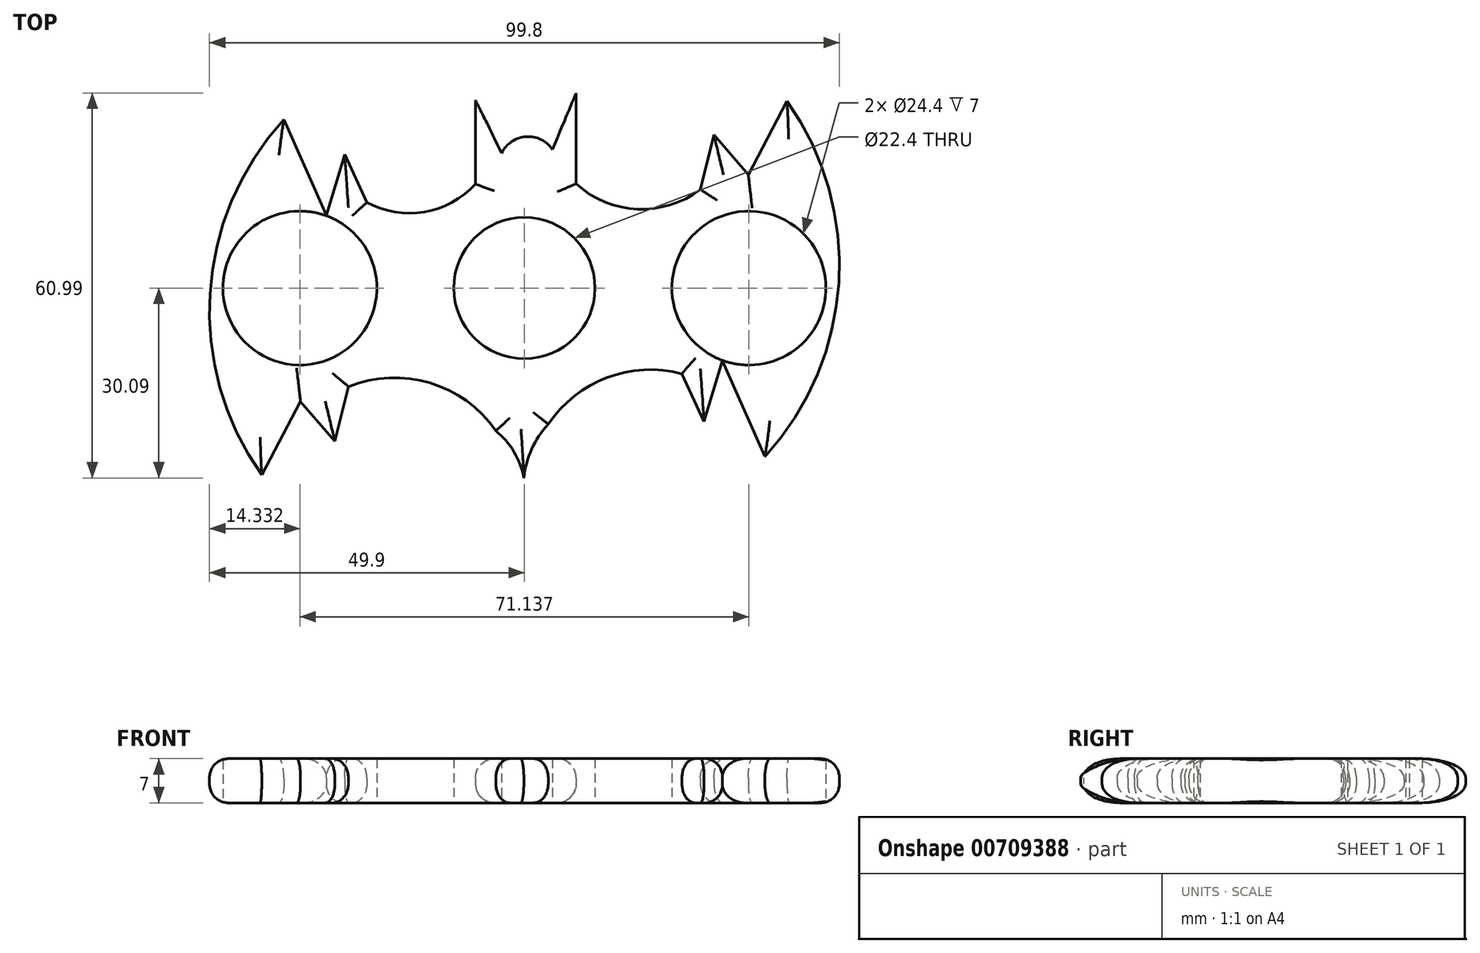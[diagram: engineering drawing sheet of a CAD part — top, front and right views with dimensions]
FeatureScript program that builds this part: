
annotation { "Feature Type Name" : "Feature", "Feature Type Description" : "" }
export const myFeature = defineFeature(function(context is Context, id is Id, definition is map)
    precondition{}
    {
        {
            var Q0;
            Q0=qCreatedBy(makeId("Top.planeOp"),FACE);
            var sketch = newSketch(context, id + "F0", { "sketchPlane" : qUnion([Q0])});
            skCircle(sketch, "E0", {"center": v(0, 0) * mm, "radius": 11.2 * mm});
            skCircle(sketch, "E1", {"center": v(0, 0) * mm, "radius": 13.2 * mm});
            skArc(sketch, "E2", {"start": v(-38.1, 26.72) * mm, "mid": v(-49.82, -0.84) * mm, "end": v(-41.61, -29.64) * mm});
            skArc(sketch, "E3.1.0", {"start": v(38.1, -26.72) * mm, "mid": v(49.82, 0.84) * mm, "end": v(41.61, 29.64) * mm});
            skLineSegment(sketch, "E4", {"start": v(-41.61, -29.64) * mm, "end": v(-35.48, -17.96) * mm});
            skLineSegment(sketch, "E5", {"start": v(-35.48, -17.96) * mm, "end": v(-35.48, -24.97) * mm});
            skArc(sketch, "E6", {"start": v(-4.53, -22.63) * mm, "mid": v(-14.98, -15.03) * mm, "end": v(-27.89, -15.62) * mm});
            skLineSegment(sketch, "E7.1.0", {"start": v(41.61, 29.64) * mm, "end": v(35.48, 17.96) * mm});
            skLineSegment(sketch, "E7.1.1", {"start": v(35.48, 17.96) * mm, "end": v(30.03, 24.29) * mm});
            skLineSegment(sketch, "E7.1.2", {"start": v(30.03, 24.29) * mm, "end": v(27.89, 15.62) * mm});
            skLineSegment(sketch, "E8", {"start": v(38.1, -26.72) * mm, "end": v(31.4, -11.53) * mm});
            skLineSegment(sketch, "E9", {"start": v(31.4, -11.53) * mm, "end": v(28.47, -21.17) * mm});
            skLineSegment(sketch, "E10", {"start": v(28.47, -21.17) * mm, "end": v(24.97, -13.58) * mm});
            skArc(sketch, "E11.1.0", {"start": v(-24.97, 13.58) * mm, "mid": v(-15.85, 12.08) * mm, "end": v(-7.74, 16.5) * mm});
            skLineSegment(sketch, "E11.1.2", {"start": v(-28.47, 21.17) * mm, "end": v(-24.97, 13.58) * mm});
            skLineSegment(sketch, "E11.1.4", {"start": v(-31.4, 11.53) * mm, "end": v(-28.47, 21.17) * mm});
            skLineSegment(sketch, "E11.1.5", {"start": v(-38.1, 26.72) * mm, "end": v(-31.4, 11.53) * mm});
            skArc(sketch, "E12", {"start": v(0, -34.06) * mm, "mid": v(-0.76, -27.75) * mm, "end": v(-4.53, -22.63) * mm});
            skArc(sketch, "E13.1.0", {"start": v(8.2, 16.53) * mm, "mid": v(17.88, 12.52) * mm, "end": v(27.89, 15.62) * mm});
            skLineSegment(sketch, "E14", {"start": v(-7.74, 16.5) * mm, "end": v(-7.74, 29.75) * mm});
            skLineSegment(sketch, "E15", {"start": v(-7.74, 29.75) * mm, "end": v(-3.6, 21.41) * mm});
            skLineSegment(sketch, "E16", {"start": v(8.2, 16.53) * mm, "end": v(8.2, 30.9) * mm});
            skLineSegment(sketch, "E17", {"start": v(8.2, 30.9) * mm, "end": v(4.45, 21.97) * mm});
            skArc(sketch, "E18", {"start": v(4.45, 21.97) * mm, "mid": v(0.27, 24) * mm, "end": v(-3.6, 21.41) * mm});
            skArc(sketch, "E19", {"start": v(24.97, -13.58) * mm, "mid": v(13.1, -14.2) * mm, "end": v(3.78, -21.57) * mm});
            skArc(sketch, "E20", {"start": v(3.78, -21.57) * mm, "mid": v(0.47, -27.38) * mm, "end": v(0, -34.06) * mm});
            skLineSegment(sketch, "E21.1.0", {"start": v(-35.48, -17.96) * mm, "end": v(-30.03, -24.29) * mm});
            skLineSegment(sketch, "E21.1.1", {"start": v(-30.03, -24.29) * mm, "end": v(-27.89, -15.62) * mm});
            skCircle(sketch, "E22", {"center": v(35.57, 0) * mm, "radius": 12.2 * mm});
            skCircle(sketch, "E23", {"center": v(-35.57, 0) * mm, "radius": 12.2 * mm});
            skSolve(sketch);
        }
        {
            var Q0;
            Q0=makeQuery(id+"F0.imprint","IMPRINT",FACE,{"disambiguationData":[TD([[makeQuery(id+"F0.imprint","IMPRINT",EDGE,{"derivedFrom":sQuery(id+"F0.wireOp",EDGE,"E0")}),-1.0]])]});
            var Q1;
            Q1=makeQuery(id+"F0.imprint","IMPRINT",FACE,{"disambiguationData":[TD([[makeQuery(id+"F0.imprint","IMPRINT",EDGE,{"derivedFrom":sQuery(id+"F0.wireOp",EDGE,"E1")}),-1.0]])]});
            extrude(context, id + "F1", {"entities" : qUnion([Q0, Q1]), "depth" : 7 * mm, "offsetDistance" : 25 * mm});
        }
        {
            var Q0;
            Q0=makeQuery(id+"F1.opExtrude","CAP_EDGE",EDGE,{"disambiguationData":[OSD([sQuery(id+"F0.wireOp",EDGE,"E20")])],"isStart":false});
            var Q1;
            Q1=makeQuery(id+"F1.opExtrude","CAP_EDGE",EDGE,{"disambiguationData":[OSD([sQuery(id+"F0.wireOp",EDGE,"E19")])],"isStart":false});
            var Q2;
            Q2=makeQuery(id+"F1.opExtrude","CAP_EDGE",EDGE,{"disambiguationData":[OSD([sQuery(id+"F0.wireOp",EDGE,"E9")])],"isStart":false});
            var Q3;
            Q3=makeQuery(id+"F1.opExtrude","CAP_EDGE",EDGE,{"disambiguationData":[OSD([sQuery(id+"F0.wireOp",EDGE,"E3.1.0")])],"isStart":false});
            var Q4;
            Q4=makeQuery(id+"F1.opExtrude","CAP_EDGE",EDGE,{"disambiguationData":[OSD([sQuery(id+"F0.wireOp",EDGE,"E8")])],"isStart":false});
            var Q5;
            Q5=makeQuery(id+"F1.opExtrude","CAP_EDGE",EDGE,{"disambiguationData":[OSD([sQuery(id+"F0.wireOp",EDGE,"E7.1.0")])],"isStart":false});
            var Q6;
            Q6=makeQuery(id+"F1.opExtrude","CAP_EDGE",EDGE,{"disambiguationData":[OSD([sQuery(id+"F0.wireOp",EDGE,"E7.1.1")])],"isStart":false});
            var Q7;
            Q7=makeQuery(id+"F1.opExtrude","CAP_EDGE",EDGE,{"disambiguationData":[OSD([sQuery(id+"F0.wireOp",EDGE,"E7.1.2")])],"isStart":false});
            var Q8;
            Q8=makeQuery(id+"F1.opExtrude","CAP_EDGE",EDGE,{"disambiguationData":[OSD([sQuery(id+"F0.wireOp",EDGE,"E13.1.0")])],"isStart":false});
            var Q9;
            Q9=makeQuery(id+"F1.opExtrude","CAP_EDGE",EDGE,{"disambiguationData":[OSD([sQuery(id+"F0.wireOp",EDGE,"E16")])],"isStart":false});
            var Q10;
            Q10=makeQuery(id+"F1.opExtrude","CAP_EDGE",EDGE,{"disambiguationData":[OSD([sQuery(id+"F0.wireOp",EDGE,"E14")])],"isStart":false});
            var Q11;
            Q11=makeQuery(id+"F1.opExtrude","CAP_EDGE",EDGE,{"disambiguationData":[OSD([sQuery(id+"F0.wireOp",EDGE,"E11.1.0")])],"isStart":false});
            var Q12;
            Q12=makeQuery(id+"F1.opExtrude","CAP_EDGE",EDGE,{"disambiguationData":[OSD([sQuery(id+"F0.wireOp",EDGE,"E11.1.2")])],"isStart":false});
            var Q13;
            Q13=makeQuery(id+"F1.opExtrude","CAP_EDGE",EDGE,{"disambiguationData":[OSD([sQuery(id+"F0.wireOp",EDGE,"E11.1.5")])],"isStart":false});
            var Q14;
            Q14=makeQuery(id+"F1.opExtrude","CAP_EDGE",EDGE,{"disambiguationData":[OSD([sQuery(id+"F0.wireOp",EDGE,"E11.1.4")])],"isStart":false});
            var Q15;
            Q15=makeQuery(id+"F1.opExtrude","CAP_EDGE",EDGE,{"disambiguationData":[OSD([sQuery(id+"F0.wireOp",EDGE,"E2")])],"isStart":false});
            var Q16;
            Q16=makeQuery(id+"F1.opExtrude","CAP_EDGE",EDGE,{"disambiguationData":[OSD([sQuery(id+"F0.wireOp",EDGE,"E4")])],"isStart":false});
            var Q17;
            Q17=makeQuery(id+"F1.opExtrude","CAP_EDGE",EDGE,{"disambiguationData":[OSD([sQuery(id+"F0.wireOp",EDGE,"wEF84jsq-XExs-cQrN-D3yr-Ib7uIkRzdJAm")])],"isStart":false});
            var Q18;
            Q18=makeQuery(id+"F1.opExtrude","CAP_EDGE",EDGE,{"disambiguationData":[OSD([sQuery(id+"F0.wireOp",EDGE,"E12")])],"isStart":false});
            var Q19;
            Q19=makeQuery(id+"F1.opExtrude","CAP_EDGE",EDGE,{"disambiguationData":[OSD([sQuery(id+"F0.wireOp",EDGE,"E5")])],"isStart":false});
            var Q20;
            Q20=makeQuery(id+"F1.opExtrude","CAP_EDGE",EDGE,{"disambiguationData":[OSD([sQuery(id+"F0.wireOp",EDGE,"E10")])],"isStart":false});
            var Q21;
            Q21=makeQuery(id+"F1.opExtrude","CAP_EDGE",EDGE,{"disambiguationData":[OSD([sQuery(id+"F0.wireOp",EDGE,"E21.1.1")])],"isStart":false});
            var Q22;
            Q22=makeQuery(id+"F1.opExtrude","CAP_EDGE",EDGE,{"disambiguationData":[OSD([sQuery(id+"F0.wireOp",EDGE,"E6")])],"isStart":false});
            var Q23;
            Q23=makeQuery(id+"F1.opExtrude","CAP_EDGE",EDGE,{"disambiguationData":[OSD([sQuery(id+"F0.wireOp",EDGE,"E21.1.0")])],"isStart":false});
            var Q24;
            Q24=makeQuery(id+"F1.opExtrude","CAP_EDGE",EDGE,{"disambiguationData":[OSD([sQuery(id+"F0.wireOp",EDGE,"E3.1.0")])],"isStart":true});
            var Q25;
            Q25=makeQuery(id+"F1.opExtrude","CAP_EDGE",EDGE,{"disambiguationData":[OSD([sQuery(id+"F0.wireOp",EDGE,"E8")])],"isStart":true});
            var Q26;
            Q26=makeQuery(id+"F1.opExtrude","CAP_EDGE",EDGE,{"disambiguationData":[OSD([sQuery(id+"F0.wireOp",EDGE,"E9")])],"isStart":true});
            var Q27;
            Q27=makeQuery(id+"F1.opExtrude","CAP_EDGE",EDGE,{"disambiguationData":[OSD([sQuery(id+"F0.wireOp",EDGE,"E10")])],"isStart":true});
            var Q28;
            Q28=makeQuery(id+"F1.opExtrude","CAP_EDGE",EDGE,{"disambiguationData":[OSD([sQuery(id+"F0.wireOp",EDGE,"E19")])],"isStart":true});
            var Q29;
            Q29=makeQuery(id+"F1.opExtrude","CAP_EDGE",EDGE,{"disambiguationData":[OSD([sQuery(id+"F0.wireOp",EDGE,"E6")])],"isStart":true});
            var Q30;
            Q30=makeQuery(id+"F1.opExtrude","CAP_EDGE",EDGE,{"disambiguationData":[OSD([sQuery(id+"F0.wireOp",EDGE,"E12")])],"isStart":true});
            var Q31;
            Q31=makeQuery(id+"F1.opExtrude","CAP_EDGE",EDGE,{"disambiguationData":[OSD([sQuery(id+"F0.wireOp",EDGE,"E20")])],"isStart":true});
            var Q32;
            Q32=makeQuery(id+"F1.opExtrude","CAP_EDGE",EDGE,{"disambiguationData":[OSD([sQuery(id+"F0.wireOp",EDGE,"E21.1.1")])],"isStart":true});
            var Q33;
            Q33=makeQuery(id+"F1.opExtrude","CAP_EDGE",EDGE,{"disambiguationData":[OSD([sQuery(id+"F0.wireOp",EDGE,"E21.1.0")])],"isStart":true});
            var Q34;
            Q34=makeQuery(id+"F1.opExtrude","CAP_EDGE",EDGE,{"disambiguationData":[OSD([sQuery(id+"F0.wireOp",EDGE,"E4")])],"isStart":true});
            var Q35;
            Q35=makeQuery(id+"F1.opExtrude","CAP_EDGE",EDGE,{"disambiguationData":[OSD([sQuery(id+"F0.wireOp",EDGE,"E2")])],"isStart":true});
            var Q36;
            Q36=makeQuery(id+"F1.opExtrude","CAP_EDGE",EDGE,{"disambiguationData":[OSD([sQuery(id+"F0.wireOp",EDGE,"E11.1.5")])],"isStart":true});
            var Q37;
            Q37=makeQuery(id+"F1.opExtrude","CAP_EDGE",EDGE,{"disambiguationData":[OSD([sQuery(id+"F0.wireOp",EDGE,"E11.1.4")])],"isStart":true});
            var Q38;
            Q38=makeQuery(id+"F1.opExtrude","CAP_EDGE",EDGE,{"disambiguationData":[OSD([sQuery(id+"F0.wireOp",EDGE,"E14")])],"isStart":true});
            var Q39;
            Q39=makeQuery(id+"F1.opExtrude","CAP_EDGE",EDGE,{"disambiguationData":[OSD([sQuery(id+"F0.wireOp",EDGE,"E16")])],"isStart":true});
            var Q40;
            Q40=makeQuery(id+"F1.opExtrude","CAP_EDGE",EDGE,{"disambiguationData":[OSD([sQuery(id+"F0.wireOp",EDGE,"E13.1.0")])],"isStart":true});
            var Q41;
            Q41=makeQuery(id+"F1.opExtrude","CAP_EDGE",EDGE,{"disambiguationData":[OSD([sQuery(id+"F0.wireOp",EDGE,"E7.1.2")])],"isStart":true});
            var Q42;
            Q42=makeQuery(id+"F1.opExtrude","CAP_EDGE",EDGE,{"disambiguationData":[OSD([sQuery(id+"F0.wireOp",EDGE,"E7.1.1")])],"isStart":true});
            var Q43;
            Q43=makeQuery(id+"F1.opExtrude","CAP_EDGE",EDGE,{"disambiguationData":[OSD([sQuery(id+"F0.wireOp",EDGE,"E7.1.0")])],"isStart":true});
            var Q44;
            Q44=makeQuery(id+"F1.opExtrude","CAP_EDGE",EDGE,{"disambiguationData":[OSD([sQuery(id+"F0.wireOp",EDGE,"E11.1.0")])],"isStart":true});
            var Q45;
            Q45=makeQuery(id+"F1.opExtrude","CAP_EDGE",EDGE,{"disambiguationData":[OSD([sQuery(id+"F0.wireOp",EDGE,"E11.1.2")])],"isStart":true});
            fillet(context, id + "F2", {"entities" : qUnion([Q0, Q1, Q2, Q3, Q4, Q5, Q6, Q7, Q8, Q9, Q10, Q11, Q12, Q13, Q14, Q15, Q16, Q17, Q18, Q19, Q20, Q21, Q22, Q23, Q24, Q25, Q26, Q27, Q28, Q29, Q30, Q31, Q32, Q33, Q34, Q35, Q36, Q37, Q38, Q39, Q40, Q41, Q42, Q43, Q44, Q45]), "radius" : 3 * mm, "tangentPropagation" : true, "allowEdgeOverflow" : false});
        }
    });
